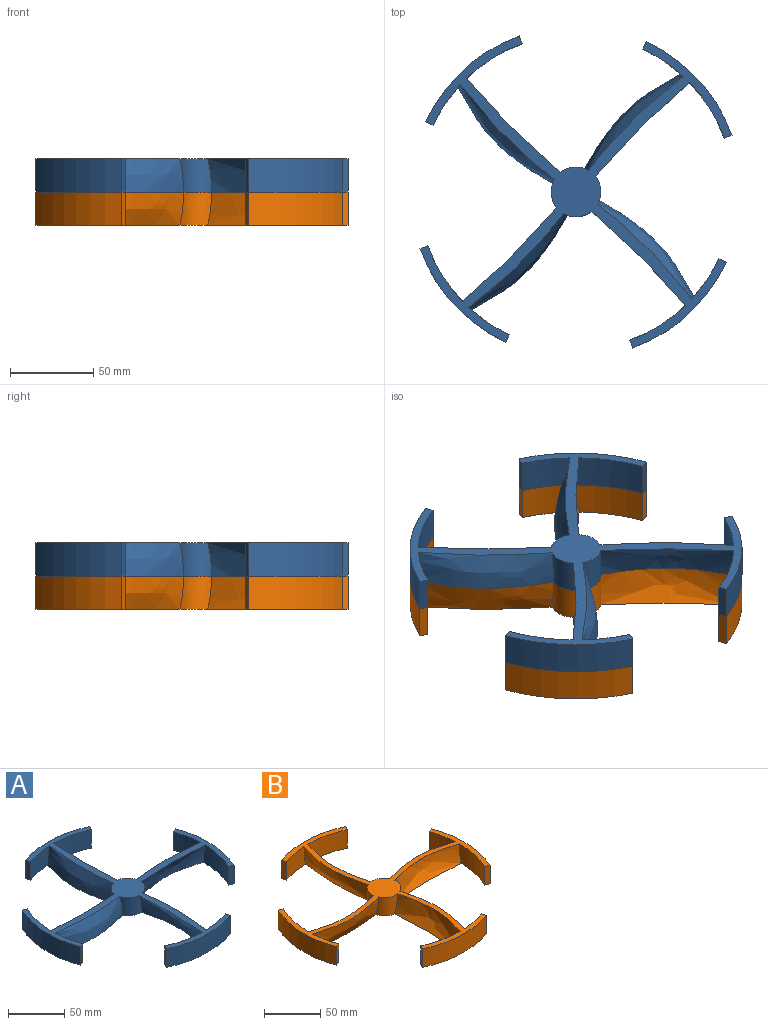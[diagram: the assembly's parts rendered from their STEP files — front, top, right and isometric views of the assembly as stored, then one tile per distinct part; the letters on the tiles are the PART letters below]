
ASSEMBLY  parts=2 mates=1
PART A: 34 faces, bbox 200.4x200.4x20.4 mm
  f0: cylinder r=15mm len=20mm, axis (0,0,-1), area 366.7mm2, adj f3,f4,f6,f14
  f1: cylinder r=15mm len=20mm, axis (0,0,-1), area 366.7mm2, adj f3,f4,f7,f21
  f2: cylinder r=15mm len=20mm, axis (0,0,-1), area 366.7mm2, adj f3,f4,f13,f23
  f3: plane 200.42x200.42mm, normal (0,0,1), area 4211.3mm2, adj f0,f1,f2,f5,f6,f7,f8,f9
  f4: plane 200.29x200.29mm, normal (0,0,-1), area 3850.5mm2, adj f0,f1,f2,f5,f6,f7,f8,f9
  f5: cylinder r=15mm len=20mm, axis (0,0,-1), area 366.7mm2, adj f3,f4,f20,f22
  f6: bspline ~81.35x20mm, area 1709.6mm2, adj f0,f3,f4,f29
  f7: bspline ~80.1x20mm, area 1727.7mm2, adj f1,f3,f4,f30
  f8: cylinder r=95mm len=28.78mm, axis (0,0,-1), area 568.9mm2, adj f3,f4,f9,f13
  f9: plane 20x4.7mm, normal (-0.34,0.94,0), area 100mm2, adj f3,f4,f8,f10
  f10: cylinder r=100mm len=76.46mm, axis (0,0,-1), area 1570.8mm2, adj f3,f4,f9,f11
  f11: plane 20x4.53mm, normal (-0.42,-0.91,0), area 100mm2, adj f3,f4,f10,f12
  f12: cylinder r=95mm len=40.82mm, axis (0,0,-1), area 818.3mm2, adj f3,f4,f11,f14
  f13: bspline ~81.35x20mm, area 1709.6mm2, adj f2,f3,f4,f8
  f14: bspline ~80.1x20mm, area 1727.7mm2, adj f0,f3,f4,f12
  f15: cylinder r=95mm len=28.78mm, axis (0,0,-1), area 568.9mm2, adj f3,f4,f16,f21
  f16: plane 20x4.7mm, normal (0.34,-0.94,0), area 100mm2, adj f3,f4,f15,f17
  f17: cylinder r=100mm len=76.46mm, axis (0,0,-1), area 1570.8mm2, adj f3,f4,f16,f18
  f18: plane 20x4.53mm, normal (0.42,0.91,0), area 100mm2, adj f3,f4,f17,f19
  f19: cylinder r=95mm len=40.82mm, axis (0,0,-1), area 818.3mm2, adj f3,f4,f18,f20
  f20: bspline ~80.1x20mm, area 1727.7mm2, adj f3,f4,f5,f19
  f21: bspline ~81.35x20mm, area 1709.6mm2, adj f1,f3,f4,f15
  f22: bspline ~81.35x20mm, area 1709.6mm2, adj f3,f4,f5,f24
  f23: bspline ~80.1x20mm, area 1727.7mm2, adj f2,f3,f4,f28
  f24: cylinder r=95mm len=28.78mm, axis (0,0,-1), area 568.9mm2, adj f3,f4,f22,f27
  f25: plane 20x4.53mm, normal (0.91,-0.42,0), area 100mm2, adj f3,f4,f26,f28
  f26: cylinder r=100mm len=76.46mm, axis (0,0,-1), area 1570.8mm2, adj f3,f4,f25,f27
  f27: plane 20x4.7mm, normal (-0.94,-0.34,0), area 100mm2, adj f3,f4,f24,f26
  f28: cylinder r=95mm len=40.82mm, axis (0,0,-1), area 818.3mm2, adj f3,f4,f23,f25
  f29: cylinder r=95mm len=28.78mm, axis (0,0,-1), area 568.9mm2, adj f3,f4,f6,f33
  f30: cylinder r=95mm len=40.82mm, axis (0,0,-1), area 818.3mm2, adj f3,f4,f7,f31
  f31: plane 20x4.53mm, normal (-0.91,0.42,0), area 100mm2, adj f3,f4,f30,f32
  f32: cylinder r=100mm len=76.46mm, axis (0,0,-1), area 1570.8mm2, adj f3,f4,f31,f33
  f33: plane 20x4.7mm, normal (0.94,0.34,0), area 100mm2, adj f3,f4,f29,f32
PART B: 34 faces, bbox 200.4x200.4x20.4 mm
  f0: cylinder r=15mm len=20mm, axis (0,0,-1), area 366.7mm2, adj f24,f25,f28,f33
  f1: cylinder r=15mm len=20mm, axis (0,0,-1), area 366.7mm2, adj f24,f26,f30,f33
  f2: cylinder r=15mm len=20mm, axis (0,0,-1), area 366.7mm2, adj f24,f27,f32,f33
  f3: cylinder r=15mm len=20mm, axis (0,0,-1), area 366.7mm2, adj f24,f29,f31,f33
  f4: cylinder r=95mm len=28.78mm, axis (0,0,-1), area 568.9mm2, adj f5,f24,f27,f33
  f5: plane 20x4.7mm, normal (-0.34,0.94,0), area 100mm2, adj f4,f6,f24,f33
  f6: cylinder r=100mm len=76.46mm, axis (0,0,-1), area 1570.8mm2, adj f5,f7,f24,f33
  f7: plane 20x4.53mm, normal (-0.42,-0.91,0), area 100mm2, adj f6,f8,f24,f33
  f8: cylinder r=95mm len=40.82mm, axis (0,0,-1), area 818.3mm2, adj f7,f24,f28,f33
  f9: cylinder r=95mm len=28.78mm, axis (0,0,-1), area 568.9mm2, adj f10,f24,f30,f33
  f10: plane 20x4.7mm, normal (0.34,-0.94,0), area 100mm2, adj f9,f11,f24,f33
  f11: cylinder r=100mm len=76.46mm, axis (0,0,-1), area 1570.8mm2, adj f10,f12,f24,f33
  f12: plane 20x4.53mm, normal (0.42,0.91,0), area 100mm2, adj f11,f13,f24,f33
  f13: cylinder r=95mm len=40.82mm, axis (0,0,-1), area 818.3mm2, adj f12,f24,f29,f33
  f14: cylinder r=95mm len=28.78mm, axis (0,0,-1), area 568.9mm2, adj f17,f24,f31,f33
  f15: plane 20x4.53mm, normal (0.91,-0.42,0), area 100mm2, adj f16,f18,f24,f33
  f16: cylinder r=100mm len=76.46mm, axis (0,0,-1), area 1570.8mm2, adj f15,f17,f24,f33
  f17: plane 20x4.7mm, normal (-0.94,-0.34,0), area 100mm2, adj f14,f16,f24,f33
  f18: cylinder r=95mm len=40.82mm, axis (0,0,-1), area 818.3mm2, adj f15,f24,f32,f33
  f19: cylinder r=95mm len=28.78mm, axis (0,0,-1), area 568.9mm2, adj f23,f24,f25,f33
  f20: cylinder r=95mm len=40.82mm, axis (0,0,-1), area 818.3mm2, adj f21,f24,f26,f33
  f21: plane 20x4.53mm, normal (-0.91,0.42,0), area 100mm2, adj f20,f22,f24,f33
  f22: cylinder r=100mm len=76.46mm, axis (0,0,-1), area 1570.8mm2, adj f21,f23,f24,f33
  f23: plane 20x4.7mm, normal (0.94,0.34,0), area 100mm2, adj f19,f22,f24,f33
  f24: plane 200.42x200.42mm, normal (0,0,-1), area 4211.3mm2, adj f0,f1,f2,f3,f4,f5,f6,f7
  f25: bspline ~81.35x20mm, area 1709.6mm2, adj f0,f19,f24,f33
  f26: bspline ~80.1x20mm, area 1727.7mm2, adj f1,f20,f24,f33
  f27: bspline ~81.35x20mm, area 1709.6mm2, adj f2,f4,f24,f33
  f28: bspline ~80.1x20mm, area 1727.7mm2, adj f0,f8,f24,f33
  f29: bspline ~80.1x20mm, area 1727.7mm2, adj f3,f13,f24,f33
  f30: bspline ~81.35x20mm, area 1709.6mm2, adj f1,f9,f24,f33
  f31: bspline ~81.35x20mm, area 1709.6mm2, adj f3,f14,f24,f33
  f32: bspline ~80.1x20mm, area 1727.7mm2, adj f2,f18,f24,f33
  f33: plane 200.3x200.3mm, normal (0,0,1), area 3845.6mm2, adj f0,f1,f2,f3,f4,f5,f6,f7
PLACE A rot(axis=(0,0,1),45deg) t=(53.55,124.51,-13.72)mm
PLACE B rot(axis=(0,0,-1),45deg) t=(53.55,124.51,-13.72)mm
MATE fastened A.f4 <-> B.f33  axis (0,0,-1) through (12.34,36.14,-13.72)mm
